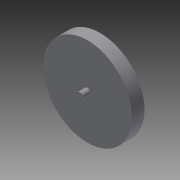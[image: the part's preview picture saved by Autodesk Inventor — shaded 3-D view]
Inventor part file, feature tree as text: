
AUTODESK INVENTOR PART (.ipt)
format: ipt  version: 2013 (Build 170138000, 138)  size: 87,040 bytes
history: native  units: mm
features: extrude x4, sketch x4, other x1
ambient origin geometry x8: Origin, YZ Plane, XZ Plane, XY Plane, X Axis, Y Axis, Z Axis, Center Point
feature tree (9):
  other  "ソリッド1"
  extrude  "押し出し1"  Depth=25.0mm
  extrude  "押し出し2"  Depth=5.0mm TaperAngle=0.0deg
  extrude  "押し出し3"  Depth=2.5mm
  extrude  "押し出し4"  Depth=3.0mm TaperAngle=0.0deg
  sketch  "スケッチ1"
  sketch  "スケッチ2"
  sketch  "スケッチ3"
  sketch  "スケッチ4"
